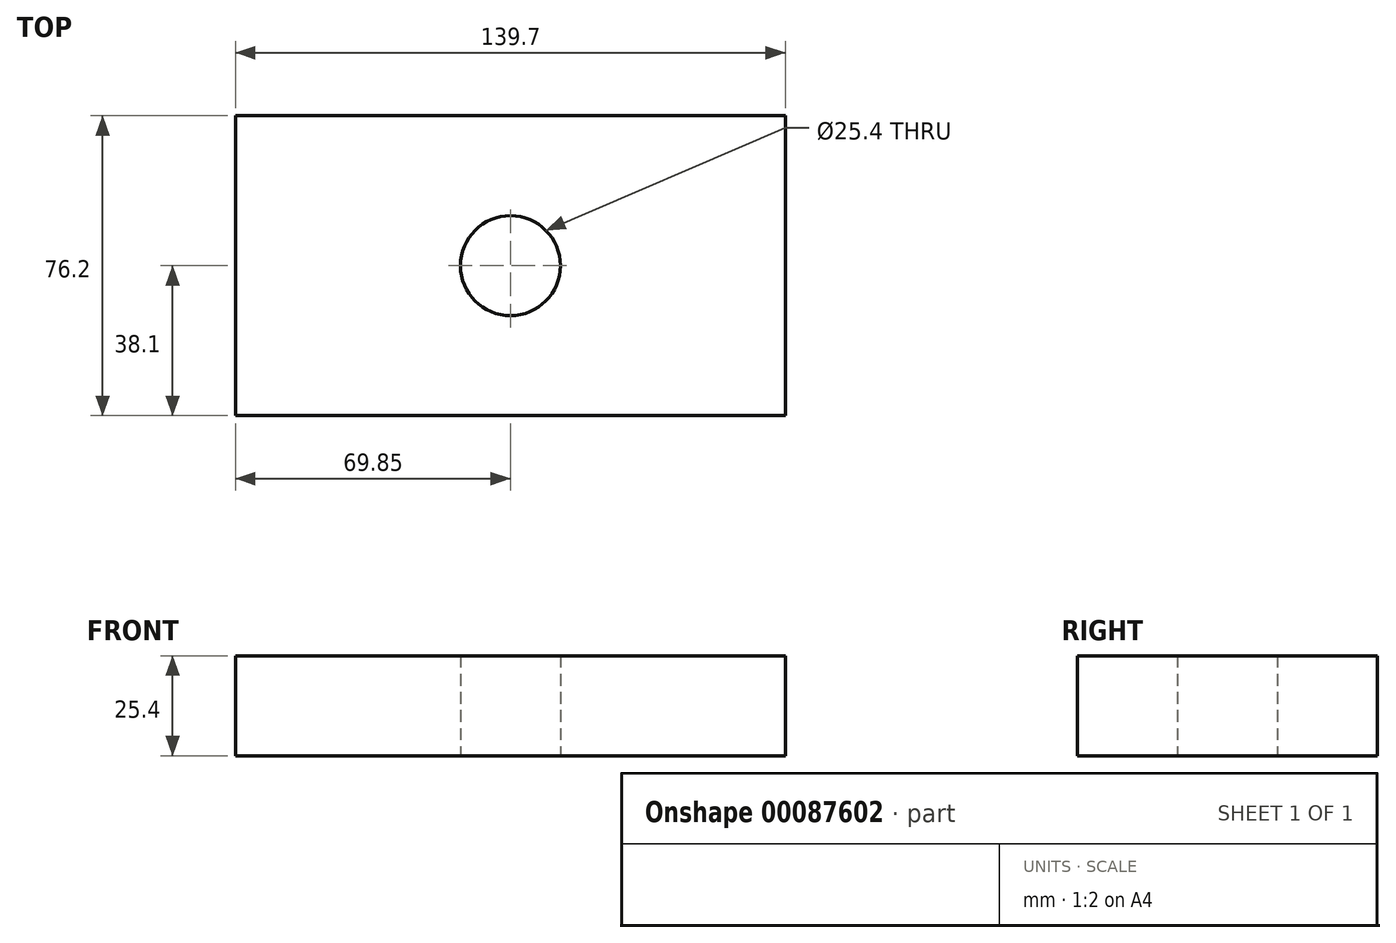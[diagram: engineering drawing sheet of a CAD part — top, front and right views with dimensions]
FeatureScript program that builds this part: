
annotation { "Feature Type Name" : "Feature", "Feature Type Description" : "" }
export const myFeature = defineFeature(function(context is Context, id is Id, definition is map)
    precondition{}
    {
        {
            var Q0;
            Q0=qCreatedBy(makeId("Top.planeOp"),FACE);
            var sketch = newSketch(context, id + "F0", { "sketchPlane" : qUnion([Q0])});
            skLineSegment(sketch, "E0.bottom", {"start": v(0, 0) * mm, "end": v(139.7, 0) * mm});
            skLineSegment(sketch, "E0.top", {"start": v(0, 76.2) * mm, "end": v(139.7, 76.2) * mm});
            skLineSegment(sketch, "E0.left", {"start": v(0, 0) * mm, "end": v(0, 76.2) * mm});
            skLineSegment(sketch, "E0.right", {"start": v(139.7, 0) * mm, "end": v(139.7, 76.2) * mm});
            skCircle(sketch, "E1", {"center": v(69.85, 38.1) * mm, "radius": 12.7 * mm});
            skSolve(sketch);
        }
        {
            var Q0;
            Q0 = qSketchRegion(id + "F0", true);
            extrude(context, id + "F1", {"entities" : qUnion([Q0]), "depth" : 25.4 * mm});
        }
    });
